# Revit family: HERZ Strömax клапан балансировочный с измерительными клапанами 4217 GM (LF-MF)
name_source: partatom
category: Rohrzubehör
units: mm (PartAtom-declared; Revit-internal decimal feet)

## family parameters
Arbeitsebenenbasiert = Nein
Beim Laden mit Abzugskörper schneiden = Nein
Bemaßung runder Anschluss = Durchmesser verwenden
Gemeinsam genutzt = Nein
Immer vertikal = Ja
OmniClass-Nummer = 23.65.55.14
OmniClass-Titel = Valves for Liquid Services
Teiletyp = Unterbricht

## types (2) — shared parameters
D04 = 9 mm  [stored 0.0295276 ft]
H03 = 10 mm  [stored 0.0328084 ft]
Hersteller = HERZ Armaturen Ges.m.b.H.
MD01 = 9.5 mm  [stored 0.031168 ft]
S02 = 60 mm  [stored 0.19685 ft]
SCRNCODE = 05;07;02
SCRNSEQ = ARM;ARM_TYP="STRV";2
URL = www.herz-armaturen.ru
W01 = 30.00°
W02 = 60.00°
Измерение перепада давления = Клапаны STRÖMAX-GM оснащен двумя измерительными клапанами:
с помощью измерительного прибора можно измерить перепад давления и по нему определить текущий расход в зависимости от степени преднастройки.
HERZ Измерительный компьютер (1 8900 05) позволяет напрямую считывать расход (см. руководство к измерительным приборам).
Исполнение = STRÖMAX-GM Балансировочный клапан с измерительными клапанами, 1/2′′ – 3′′.
Исполнение с прямым невыдвижным шпинделем, муфта х муфта, латунный корпус без покрытия, уплотнение шпинделя двойным кольцевым уплотнением O-Ring, преднастройка посредством ограничения хода внутреннего шпинделя, цифровые показания степени настройки отображаются в окне маховика.
Два измерительных клапана расположены рядом с маховиком.
Корпус = латунь, устойчивая к селективной цинковой коррозии
Макс. рабочая температура (до DN32) = 130 °C
Макс. рабочая температура (с DN40) = 110 °C
Макс. рабочее давление = 1600000.0 Pa
Область применения = Балансировочные клапаны применяются для гидравлической балансировки систем отопления и охлаждения, регулировки магистральных трубопроводов, стояков, теплообменников, регистров отопления и охлаждения.
Положение клапана при монтаже = Неподнимающийся шпиндель, расположенный перпендикулярно оси клапана, обеспечивает доступность и лёгкость в обслуживании в любом монтажном положении.
Среда = Качество теплоносителя в соответствии с ÖNORM H5195 и VDI 2035.
Допускается использование этилен- и пропиленгликоля в соотношении 25-50% с водой.
zero-valued in all types: SC_NennweiteBerechnet

## type names (no varying parameters)
- LF
- MF

note: [stored X ft] marks values corroborated as IEEE doubles in the binary element streams (Revit-internal decimal feet)
